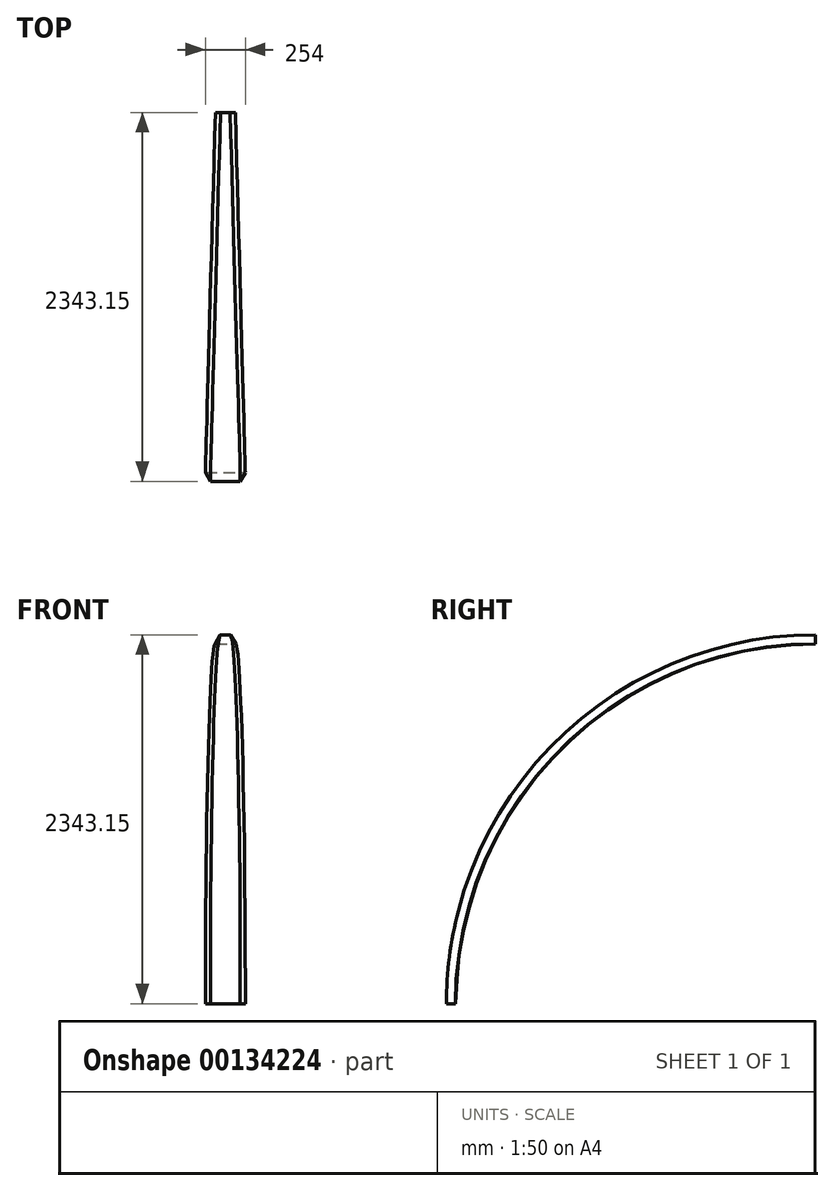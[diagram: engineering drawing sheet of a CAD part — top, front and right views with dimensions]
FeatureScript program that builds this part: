
annotation { "Feature Type Name" : "Feature", "Feature Type Description" : "" }
export const myFeature = defineFeature(function(context is Context, id is Id, definition is map)
    precondition{}
    {
        {
            var Q0;
            Q0=qCreatedBy(makeId("Right.planeOp"),FACE);
            var sketch = newSketch(context, id + "F0", { "sketchPlane" : qUnion([Q0])});
            skLineSegment(sketch, "E0", {"start": v(0, 0) * mm, "end": v(0, -2286) * mm, "construction": true});
            skLineSegment(sketch, "E1", {"start": v(0, 0) * mm, "end": v(-2286, 0) * mm, "construction": true});
            skLineSegment(sketch, "E2", {"start": v(-2286, 0) * mm, "end": v(-2286, 948.07) * mm, "construction": true});
            skLineSegment(sketch, "E3", {"start": v(0, -2286) * mm, "end": v(1396.28, -2286) * mm, "construction": true});
            skArc(sketch, "E4", {"start": v(0, -2286) * mm, "mid": v(-1616.45, -1616.45) * mm, "end": v(-2286, 0) * mm, "construction": true});
            skArc(sketch, "E5.MirrorCS", {"start": v(0, 2286) * mm, "mid": v(-1616.45, 1616.45) * mm, "end": v(-2286, 0) * mm, "construction": true});
            skLineSegment(sketch, "E6", {"start": v(0, 2648.85) * mm, "end": v(-4525.13, 0) * mm, "construction": true});
            skLineSegment(sketch, "E7", {"start": v(-2286, 0) * mm, "end": v(-4525.13, 0) * mm, "construction": true});
            skLineSegment(sketch, "E8", {"start": v(0, 2286) * mm, "end": v(0, 0) * mm, "construction": true});
            skLineSegment(sketch, "E9", {"start": v(0, -2286) * mm, "end": v(0, -7011.4) * mm, "construction": true});
            skLineSegment(sketch, "E10", {"start": v(-1154.84, -1972.85) * mm, "end": v(-634.14, -1972.85) * mm, "construction": true});
            skLineSegment(sketch, "E11", {"start": v(-634.14, -1972.85) * mm, "end": v(-634.14, -2277.65) * mm, "construction": true});
            skLineSegment(sketch, "E12", {"start": v(-634.14, -2277.65) * mm, "end": v(-1154.84, -1972.85) * mm, "construction": true});
            skLineSegment(sketch, "E13", {"start": v(-634.14, -2277.65) * mm, "end": v(4218.86, -5118.43) * mm, "construction": true});
            skLineSegment(sketch, "E14", {"start": v(-4525.13, 0) * mm, "end": v(-1154.84, -1972.85) * mm, "construction": true});
            skLineSegment(sketch, "E15", {"start": v(-634.14, -2277.65) * mm, "end": v(3010.76, -2277.65) * mm, "construction": true});
            skLineSegment(sketch, "E16", {"start": v(3010.76, -2277.65) * mm, "end": v(3010.76, -4091.22) * mm, "construction": true});
            skPoint(sketch, "E17", {"position": v(-1154.84, 1972.85) * mm});
            skLineSegment(sketch, "E18.0", {"start": v(-19.25, 2681.74) * mm, "end": v(-4544.37, 32.88) * mm});
            skSolve(sketch);
        }
        {
            var Q0;
            Q0=qCreatedBy(makeId("Top.planeOp"),FACE);
            var sketch = newSketch(context, id + "F1", { "sketchPlane" : qUnion([Q0])});
            skLineSegment(sketch, "E19", {"start": v(-127, -2286) * mm, "end": v(127, -2286) * mm});
            skLineSegment(sketch, "E20", {"start": v(127, -2286) * mm, "end": v(94, -2343.15) * mm});
            skLineSegment(sketch, "E21", {"start": v(94, -2343.15) * mm, "end": v(-94, -2343.15) * mm});
            skLineSegment(sketch, "E22", {"start": v(-94, -2343.15) * mm, "end": v(-127, -2286) * mm});
            skLineSegment(sketch, "E23", {"start": v(0, -2286) * mm, "end": v(0, -2343.15) * mm, "construction": true});
            skSolve(sketch);
        }
        {
            var Q0;
            Q0=qCreatedBy(makeId("Front.planeOp"),FACE);
            var sketch = newSketch(context, id + "F2", { "sketchPlane" : qUnion([Q0])});
            skLineSegment(sketch, "E24", {"start": v(63.5, 2286) * mm, "end": v(-63.5, 2286) * mm});
            skLineSegment(sketch, "E25", {"start": v(-63.5, 2286) * mm, "end": v(-30.5, 2343.15) * mm});
            skLineSegment(sketch, "E26", {"start": v(-30.5, 2343.15) * mm, "end": v(30.5, 2343.15) * mm});
            skLineSegment(sketch, "E27", {"start": v(30.5, 2343.15) * mm, "end": v(63.5, 2286) * mm});
            skLineSegment(sketch, "E28", {"start": v(0, 2286) * mm, "end": v(0, 2343.15) * mm, "construction": true});
            skPoint(sketch, "E28.endSnap0", {"position": v(0, 2286) * mm});
            skSolve(sketch);
        }
        {
            var Q0;
            Q0=qCreatedBy(makeId("Right.planeOp"),FACE);
            var sketch = newSketch(context, id + "F3", { "sketchPlane" : qUnion([Q0])});
            skLineSegment(sketch, "E29", {"start": v(-2286, 0) * mm, "end": v(-2286, -352.16) * mm, "construction": true});
            skArc(sketch, "E30", {"start": v(-2286, 0) * mm, "mid": v(-1616.45, 1616.45) * mm, "end": v(0, 2286) * mm});
            skSolve(sketch);
        }
        {
            var Q0;
            Q0=qCreatedBy(makeId("Front.planeOp"),FACE);
            var sketch = newSketch(context, id + "F4", { "sketchPlane" : qUnion([Q0])});
            skLineSegment(sketch, "E31", {"start": v(63.5, 2286) * mm, "end": v(63.5, 2234.92) * mm});
            skLineSegment(sketch, "E32", {"start": v(63.5, 2234.92) * mm, "end": v(181.22, 2234.92) * mm});
            skLineSegment(sketch, "E33", {"start": v(181.22, 2234.92) * mm, "end": v(181.22, 2433.28) * mm});
            skLineSegment(sketch, "E34", {"start": v(181.22, 2433.28) * mm, "end": v(-136.49, 2433.28) * mm});
            skLineSegment(sketch, "E35", {"start": v(-136.49, 2433.28) * mm, "end": v(-136.49, 2230.28) * mm});
            skLineSegment(sketch, "E36", {"start": v(-136.49, 2230.28) * mm, "end": v(-63.5, 2230.28) * mm});
            skLineSegment(sketch, "E37", {"start": v(-63.5, 2230.28) * mm, "end": v(-63.5, 2286) * mm});
            skLineSegment(sketch, "E38", {"start": v(63.5, 2286) * mm, "end": v(30.5, 2343.15) * mm});
            skLineSegment(sketch, "E39", {"start": v(30.5, 2343.15) * mm, "end": v(-30.5, 2343.15) * mm});
            skLineSegment(sketch, "E40", {"start": v(-30.5, 2343.15) * mm, "end": v(-63.5, 2286) * mm});
            skLineSegment(sketch, "E41", {"start": v(0, 2343.15) * mm, "end": v(0, 2433.28) * mm});
            skSolve(sketch);
        }
        {
            var Q0;
            Q0=sQuery(id+"F2.wireOp",VERTEX,"E25.start");
            var Q1;
            Q1=sQuery(id+"F4.wireOp",VERTEX,"E37.start");
            var Q2;
            Q2=sQuery(id+"F1.wireOp",VERTEX,"E22.end");
            cPlane(context, id + "F5", {"entities" : qUnion([Q0, Q1, Q2]), "cplaneType" : CPlaneType.THREE_POINT, "offset" : 25.4 * mm, "width" : 152.4 * mm, "height" : 152.4 * mm});
        }
        {
            var Q0;
            Q0=qCreatedBy(id+"F5.planeOp",FACE);
            var sketch = newSketch(context, id + "F6", { "sketchPlane" : qUnion([Q0])});
            skLineSegment(sketch, "E42", {"start": v(-2288.64, 0) * mm, "end": v(-2288.64, -164.6) * mm, "construction": true});
            skArc(sketch, "E43", {"start": v(-2288.64, 0) * mm, "mid": v(-1618.78, 1616.76) * mm, "end": v(-1.76, 2286) * mm});
            skSolve(sketch);
        }
        {
            var Q0;
            Q0=sQuery(id+"F4.wireOp",VERTEX,"E38.start");
            var Q1;
            Q1=sQuery(id+"F4.wireOp",VERTEX,"E32.start");
            var Q2;
            Q2=sQuery(id+"F1.wireOp",VERTEX,"E20.start");
            cPlane(context, id + "F7", {"entities" : qUnion([Q0, Q1, Q2]), "cplaneType" : CPlaneType.THREE_POINT, "offset" : 25.4 * mm, "width" : 152.4 * mm, "height" : 152.4 * mm});
        }
        {
            var Q0;
            Q0=qCreatedBy(id+"F7.planeOp",FACE);
            var sketch = newSketch(context, id + "F8", { "sketchPlane" : qUnion([Q0])});
            skLineSegment(sketch, "E44", {"start": v(-2288.64, 0) * mm, "end": v(-2288.64, -217.98) * mm, "construction": true});
            skArc(sketch, "E45", {"start": v(-2288.64, 0) * mm, "mid": v(-1618.78, 1616.76) * mm, "end": v(-1.76, 2286) * mm});
            skSolve(sketch);
        }
        {
            var Q0;
            Q0=makeQuery(id+"F1.imprint","IMPRINT",FACE,{"disambiguationData":[TD([[makeQuery(id+"F1.imprint","IMPRINT",EDGE,{"derivedFrom":sQuery(id+"F1.wireOp",EDGE,"E19")}),-1.0]])]});
            var Q1;
            Q1=sQuery(id+"F3.wireOp",EDGE,"E30");
            sweep(context, id + "F9", {"profiles" : qUnion([Q0]), "path" : qUnion([Q1])});
        }
        {
            var Q0;
            Q0=makeQuery(id+"F4.imprint","IMPRINT",FACE,{"disambiguationData":[TD([[makeQuery(id+"F4.imprint","IMPRINT",EDGE,{"derivedFrom":sQuery(id+"F4.wireOp",EDGE,"E31")}),1.0]])]});
            var Q1;
            Q1=sQuery(id+"F8.wireOp",EDGE,"E45");
            sweep(context, id + "F10", {"operationType" : NewBodyOperationType.REMOVE, "profiles" : qUnion([Q0]), "path" : qUnion([Q1])});
        }
        {
            var Q0;
            {var subQ3=sQuery(id+"F4.wireOp",EDGE,"E35");Q0=makeQuery(id+"F4.imprint","IMPRINT",FACE,{"disambiguationData":[TD([[makeQuery(id+"F4.imprint","IMPRINT",EDGE,{"derivedFrom":subQ3}),1.0]])]});}
            var Q1;
            Q1=sQuery(id+"F6.wireOp",EDGE,"E43");
            sweep(context, id + "F11", {"operationType" : NewBodyOperationType.REMOVE, "profiles" : qUnion([Q0]), "path" : qUnion([Q1])});
        }
    });
